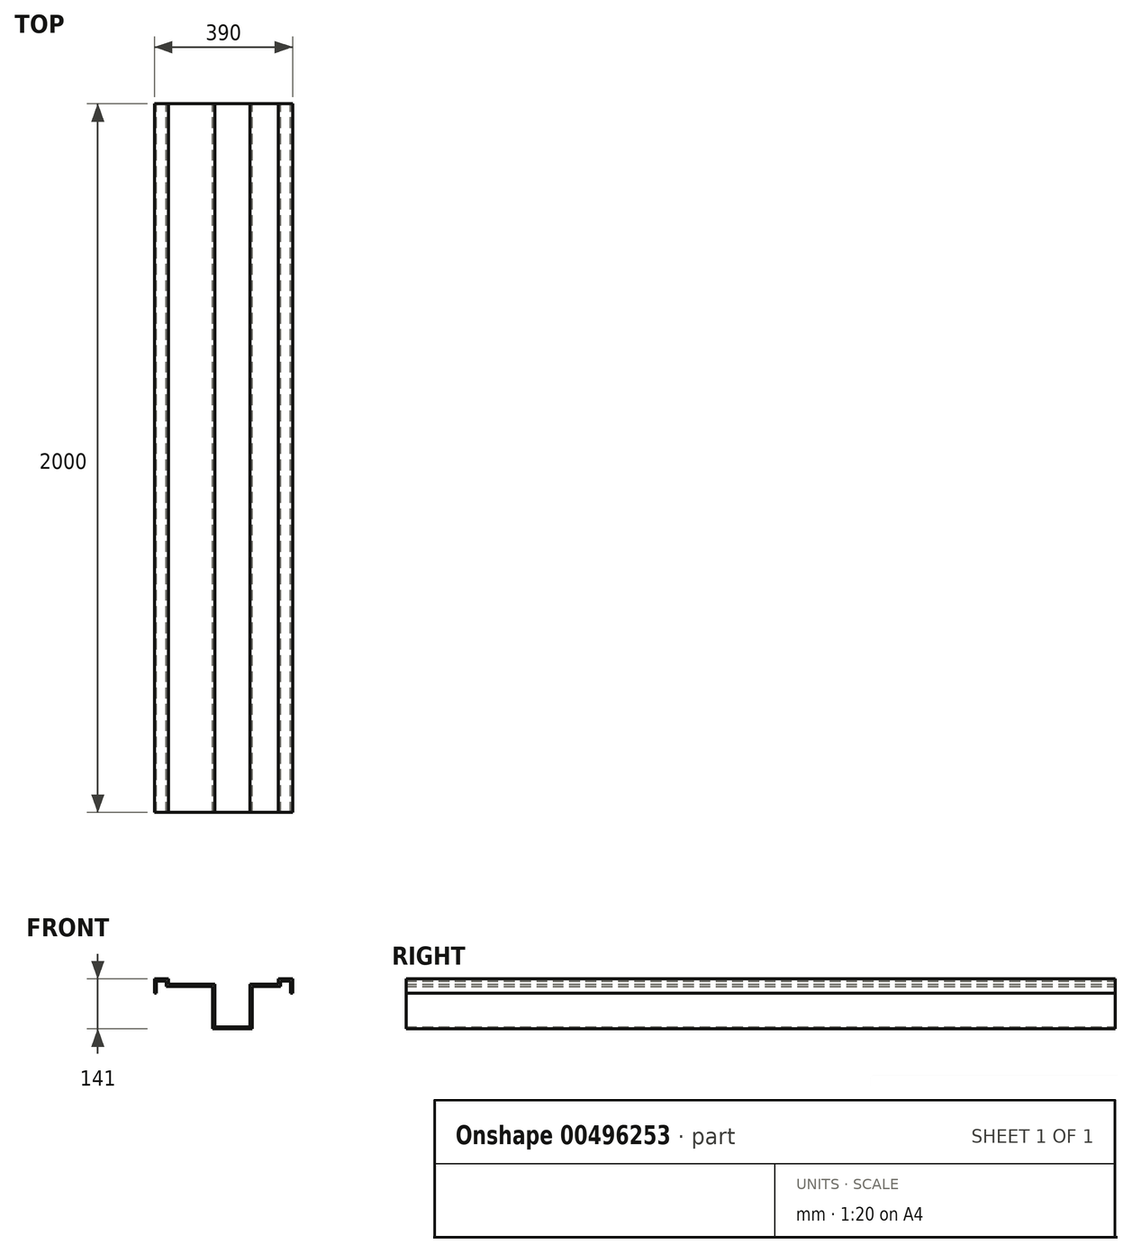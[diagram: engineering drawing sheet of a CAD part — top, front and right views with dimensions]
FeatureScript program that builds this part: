
annotation { "Feature Type Name" : "Feature", "Feature Type Description" : "" }
export const myFeature = defineFeature(function(context is Context, id is Id, definition is map)
    precondition{}
    {
        {
            var Q0;
            Q0=qCreatedBy(makeId("Front.planeOp"),FACE);
            var sketch = newSketch(context, id + "F0", { "sketchPlane" : qUnion([Q0])});
            skLineSegment(sketch, "E0", {"start": v(0, 0) * mm, "end": v(0, 40) * mm});
            skLineSegment(sketch, "E1", {"start": v(0, 40) * mm, "end": v(40, 40) * mm});
            skLineSegment(sketch, "E2", {"start": v(40, 40) * mm, "end": v(40, 25) * mm});
            skLineSegment(sketch, "E3", {"start": v(40, 25) * mm, "end": v(170, 25) * mm});
            skLineSegment(sketch, "E4", {"start": v(170, 25) * mm, "end": v(170, -95) * mm});
            skLineSegment(sketch, "E5", {"start": v(170, -95) * mm, "end": v(270, -95) * mm});
            skLineSegment(sketch, "E6", {"start": v(270, -95) * mm, "end": v(270, 25) * mm});
            skLineSegment(sketch, "E7", {"start": v(270, 25) * mm, "end": v(350, 25) * mm});
            skLineSegment(sketch, "E8", {"start": v(350, 25) * mm, "end": v(350, 40) * mm});
            skLineSegment(sketch, "E9", {"start": v(350, 40) * mm, "end": v(390, 40) * mm});
            skLineSegment(sketch, "E10", {"start": v(390, 40) * mm, "end": v(390, 0) * mm});
            skLineSegment(sketch, "E11.0", {"start": v(384, 34) * mm, "end": v(384, 0) * mm});
            skLineSegment(sketch, "E11.1", {"start": v(34, 19) * mm, "end": v(164, 19) * mm});
            skLineSegment(sketch, "E11.2", {"start": v(34, 34) * mm, "end": v(34, 19) * mm});
            skLineSegment(sketch, "E11.3", {"start": v(6, 34) * mm, "end": v(34, 34) * mm});
            skLineSegment(sketch, "E11.4", {"start": v(6, 0) * mm, "end": v(6, 34) * mm});
            skLineSegment(sketch, "E11.5", {"start": v(164, 19) * mm, "end": v(164, -101) * mm});
            skLineSegment(sketch, "E11.6", {"start": v(164, -101) * mm, "end": v(276, -101) * mm});
            skLineSegment(sketch, "E11.7", {"start": v(276, -101) * mm, "end": v(276, 19) * mm});
            skLineSegment(sketch, "E11.8", {"start": v(276, 19) * mm, "end": v(356, 19) * mm});
            skLineSegment(sketch, "E11.9", {"start": v(356, 19) * mm, "end": v(356, 34) * mm});
            skLineSegment(sketch, "E11.10", {"start": v(356, 34) * mm, "end": v(384, 34) * mm});
            skLineSegment(sketch, "E12", {"start": v(0, 0) * mm, "end": v(6, 0) * mm});
            skLineSegment(sketch, "E13", {"start": v(384, 0) * mm, "end": v(390, 0) * mm});
            skSolve(sketch);
        }
        {
            var Q0;
            Q0 = qSketchRegion(id + "F0", true);
            extrude(context, id + "F1", {"entities" : qUnion([Q0]), "depth" : 2000 * mm});
        }
    });
